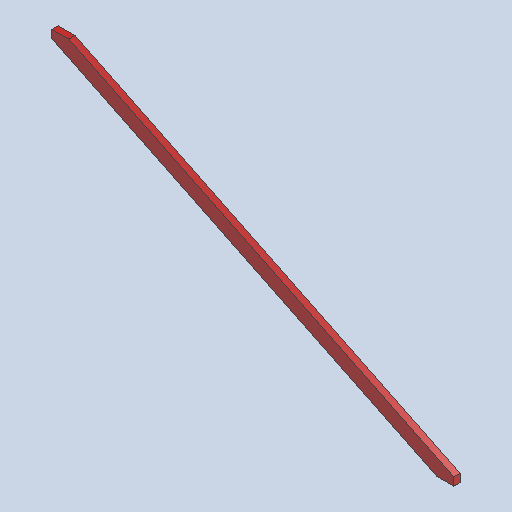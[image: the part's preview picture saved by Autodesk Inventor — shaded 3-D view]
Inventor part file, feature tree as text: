
AUTODESK INVENTOR PART (.ipt)
format: ipt  version: 2025.1 (Build 291241020, 241B)  size: 256,000 bytes
history: native  units: in
note: dims shown in document units (in); Inventor stores cm internally (conversion verified against a paired STEP export)
features: other x7, reference x4, extrude x1, sketch x1
ambient origin geometry x8: Origin, YZ Plane, XZ Plane, XY Plane, X Axis, Y Axis, Z Axis, Center Point
bodies: Solid1 (feature_tree)
feature tree (13):
  extrude  "Extrusion1"  [1 undecoded]
  sketch  "Sketch1"  dims[d2=1.5in d3=0.0in]
  reference  "Reference1"
  reference  "Reference2"
  reference  "Reference3"
  reference  "Reference4"
  other  "<userpath>\Documents\Tburn24\layer1\layer1.iam"
  other  "layer1.iam"
  other  "10'x2x4:4"
  other  "16'x2x4:2"
  other  "10'x2x4:6"
  other  "12'x2x4:1"
  other  "Finish1"
note: 1 required parameter value undecoded (feature->parameter linkage not recoverable at this tier; creation-order binding heuristic only, values carry confidence <= 0.55)
